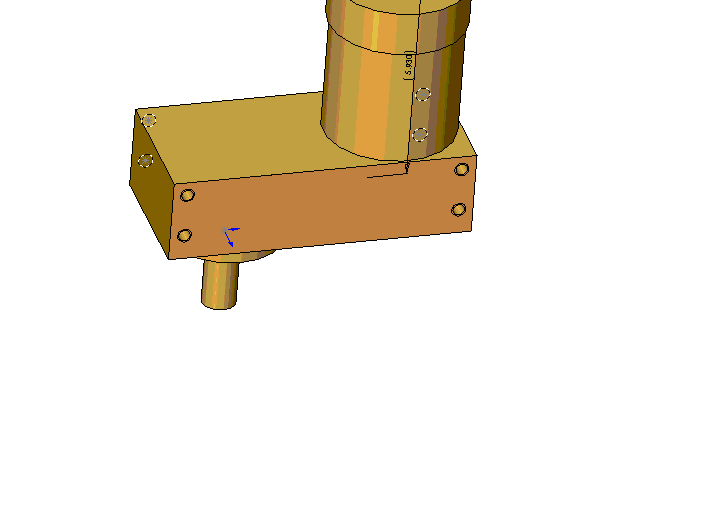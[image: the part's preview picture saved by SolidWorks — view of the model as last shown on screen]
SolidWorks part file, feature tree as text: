
SOLIDWORKS PART (.sldprt)
format: sldprt  version: not decoded by parser v0  size: 353,280 bytes
history: native  units: mm
features: sketch x10, thread x9, extrude x5, hole x2, material x1, cut_extrude x1 + 1 further entry (+11 scaffold rows collapsed)
feature tree (40):
  "Annotations"  RD1=150.622mm
  scaffold x11  (default folders/planes/origin — collapsed)
  material  "Material <not specified>"
  sketch  "Sketch1"  dims[D1=76.2mm D2=42.3672mm D3=168.275mm]
  extrude  "Extrude1"  Depth=57.15mm
  sketch  "Sketch2"  dims[D1=25.4mm]
  extrude  "Extrude2"  Depth=6.35mm
  sketch  "Sketch3"  dims[D1=19.05mm]
  extrude  "Extrude3"  Depth=38.1mm
  hole  "5/16-18 Tapped Hole1"  Diameter=6.5278mm Depth=22.9235mm
  sketch  "Sketch6"  dims[D1=152.4mm D2=7.9375mm D3=25.4mm D4=7.9375mm]
  sketch  "Sketch5"  dims[hole-wizard template sketch: 47 standard entries collapsed; hole parameters kept: c15.Tap Drill Depth=22.9235mm c15.D3=~14.816244mm c15.Drill Angle=118.0deg]
  thread  "Cosmetic Thread1"  Diameter=15.875mm  [1 undecoded]
  thread  "Cosmetic Thread2"  Diameter=15.875mm  [1 undecoded]
  thread  "Cosmetic Thread3"  Diameter=15.875mm  [1 undecoded]
  thread  "Cosmetic Thread4"  Diameter=15.875mm  [1 undecoded]
  sketch  "Sketch7"  dims[D1=73.66mm D2=38.1mm]
  extrude  "Extrude4"  Depth=68.072mm
  sketch  "Sketch8"  dims[D1=76.962mm]
  extrude  "Extrude5"  Depth=25.4mm
  hole  "5/16-18 Tapped Hole2"  Diameter=6.5278mm Depth=22.922992mm
  sketch  "Sketch10"
  sketch  "Sketch9"  dims[hole-wizard template sketch: 47 standard entries collapsed; hole parameters kept: c15.Tap Drill Depth=~22.922992mm c15.D3=~14.816244mm c15.Drill Angle=118.0deg]
  thread  "Cosmetic Thread5"  Diameter=15.875mm  [1 undecoded]
  thread  "Cosmetic Thread6"  Diameter=15.875mm  [1 undecoded]
  thread  "Cosmetic Thread7"  Diameter=15.875mm  [1 undecoded]
  thread  "Cosmetic Thread8"  Diameter=15.875mm  [1 undecoded]
  thread  "Cosmetic Thread9"  Diameter=15.875mm  [1 undecoded]
  sketch  "Sketch11"  dims[D1=33.02mm]
  cut_extrude  "Cut-Extrude1"  Depth=9.525mm
decode coverage: 26 of 27 modeling features carry decoded parameters; 1 rows unclassified (native names shown)
note: ~ marks probable driven/reference dimensions
note: 9 parameter values undecoded
note: suppression state not decoded; provenance and decode notes live in map.json
